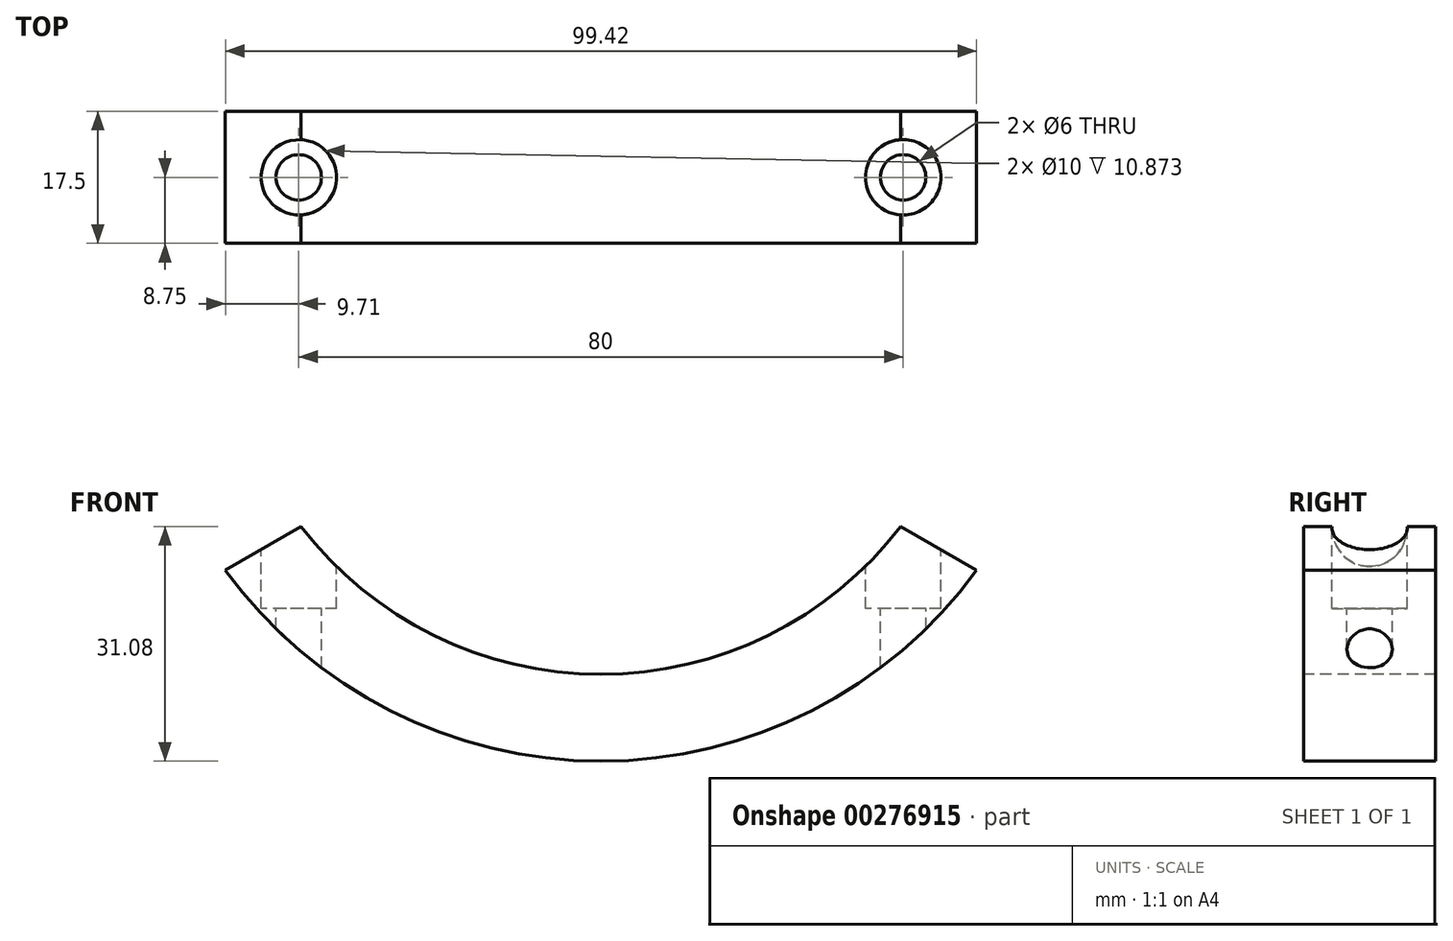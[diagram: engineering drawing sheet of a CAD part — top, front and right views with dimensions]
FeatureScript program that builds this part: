
annotation { "Feature Type Name" : "Feature", "Feature Type Description" : "" }
export const myFeature = defineFeature(function(context is Context, id is Id, definition is map)
    precondition{}
    {
        {
            var Q0;
            Q0=qCreatedBy(makeId("Front.planeOp"),FACE);
            var sketch = newSketch(context, id + "F0", { "sketchPlane" : qUnion([Q0])});
            skLineSegment(sketch, "E0", {"start": v(-39.69, 4.87) * mm, "end": v(-49.71, -0.92) * mm});
            skLineSegment(sketch, "E1", {"start": v(39.69, 4.87) * mm, "end": v(49.71, -0.92) * mm});
            skPoint(sketch, "E2", {"position": v(0, 35.29) * mm});
            skArc(sketch, "E3", {"start": v(-49.71, -0.92) * mm, "mid": v(0, -26.21) * mm, "end": v(49.71, -0.92) * mm});
            skArc(sketch, "E4", {"start": v(-39.69, 4.87) * mm, "mid": v(0, -14.71) * mm, "end": v(39.69, 4.87) * mm});
            skLineSegment(sketch, "E5", {"start": v(0, 35.29) * mm, "end": v(0, -44.65) * mm, "construction": true});
            skSolve(sketch);
        }
        {
            var Q0;
            Q0=makeQuery(id+"F0.imprint","IMPRINT",FACE,{"disambiguationData":[TD([[makeQuery(id+"F0.imprint","IMPRINT",EDGE,{"derivedFrom":sQuery(id+"F0.wireOp",EDGE,"E0")}),1.0]])]});
            extrude(context, id + "F1", {"entities" : qUnion([Q0]), "oppositeDirection" : true, "depth" : 17.5 * mm});
        }
        {
            var Q0;
            Q0=makeQuery(id+"F1.opExtrude","SWEPT_BODY",BODY,{"disambiguationData":[OSD([sQuery(id+"F0.wireOp",EDGE,"E0"),sQuery(id+"F0.wireOp",EDGE,"E1"),sQuery(id+"F0.wireOp",EDGE,"E3"),sQuery(id+"F0.wireOp",EDGE,"E4")])]});
            transform(context, id + "F2", {"entities" : qUnion([Q0]), "transformType" : TransformType.TRANSLATION_3D, "dx" : 0 * mm, "dy" : 0 * mm, "dz" : 0 * mm, "makeCopy" : true});
        }
        {
            var Q0;
            Q0=makeQuery(id+"F2.opPattern","COPY",BODY,{"derivedFrom":makeQuery(id+"F1.opExtrude","SWEPT_BODY",BODY,{"disambiguationData":[OSD([sQuery(id+"F0.wireOp",EDGE,"E0"),sQuery(id+"F0.wireOp",EDGE,"E1"),sQuery(id+"F0.wireOp",EDGE,"E3"),sQuery(id+"F0.wireOp",EDGE,"E4")])]}),"instanceName":"1"});
            deleteBodies(context, id + "F3", {"entities" : qUnion([Q0])});
        }
        {
            var Q0;
            Q0=qCreatedBy(makeId("Top.planeOp"),FACE);
            cPlane(context, id + "F4", {"entities" : qUnion([Q0]), "cplaneType" : CPlaneType.OFFSET, "offset" : 20 * mm, "width" : 150 * mm, "height" : 150 * mm});
        }
        {
            var Q0;
            Q0=qCreatedBy(id+"F4.planeOp",FACE);
            var sketch = newSketch(context, id + "F5", { "sketchPlane" : qUnion([Q0])});
            skCircle(sketch, "E6", {"center": v(40, 8.75) * mm, "radius": 3 * mm});
            skCircle(sketch, "E7", {"center": v(-40, 8.75) * mm, "radius": 3 * mm});
            skLineSegment(sketch, "E8", {"start": v(0, 0) * mm, "end": v(0, 29.1) * mm, "construction": true});
            skCircle(sketch, "E9", {"center": v(40, 8.75) * mm, "radius": 5 * mm});
            skCircle(sketch, "E10", {"center": v(-40, 8.75) * mm, "radius": 5 * mm});
            skLineSegment(sketch, "E11", {"start": v(0, 0) * mm, "end": v(87.97, 0) * mm, "construction": true});
            skSolve(sketch);
        }
        {
            var Q0;
            Q0=makeQuery(id+"F5.imprint","IMPRINT",FACE,{"disambiguationData":[TD([[makeQuery(id+"F5.imprint","IMPRINT",EDGE,{"derivedFrom":sQuery(id+"F5.wireOp",EDGE,"E6")}),1.0]])]});
            var Q1;
            Q1=makeQuery(id+"F5.imprint","IMPRINT",FACE,{"disambiguationData":[TD([[makeQuery(id+"F5.imprint","IMPRINT",EDGE,{"derivedFrom":sQuery(id+"F5.wireOp",EDGE,"E7")}),1.0]])]});
            extrude(context, id + "F6", {"entities" : qUnion([Q0, Q1]), "operationType" : NewBodyOperationType.REMOVE, "endBound" : BoundingType.THROUGH_ALL, "oppositeDirection" : true, "depth" : 25 * mm});
        }
        {
            var Q0;
            Q0=makeQuery(id+"F5.imprint","IMPRINT",FACE,{"disambiguationData":[TD([[makeQuery(id+"F5.imprint","IMPRINT",EDGE,{"derivedFrom":sQuery(id+"F5.wireOp",EDGE,"E6")}),-1.0]])]});
            var Q1;
            Q1=makeQuery(id+"F5.imprint","IMPRINT",FACE,{"disambiguationData":[TD([[makeQuery(id+"F5.imprint","IMPRINT",EDGE,{"derivedFrom":sQuery(id+"F5.wireOp",EDGE,"E7")}),-1.0]])]});
            extrude(context, id + "F7", {"entities" : qUnion([Q0, Q1]), "operationType" : NewBodyOperationType.REMOVE, "oppositeDirection" : true, "depth" : 26 * mm});
        }
        {
            var Q0;
            Q0=qCreatedBy(makeId("Right.planeOp"),FACE);
            cPlane(context, id + "F8", {"entities" : qUnion([Q0]), "cplaneType" : CPlaneType.OFFSET, "offset" : 33.5 * mm, "width" : 150 * mm, "height" : 150 * mm});
        }
    });
